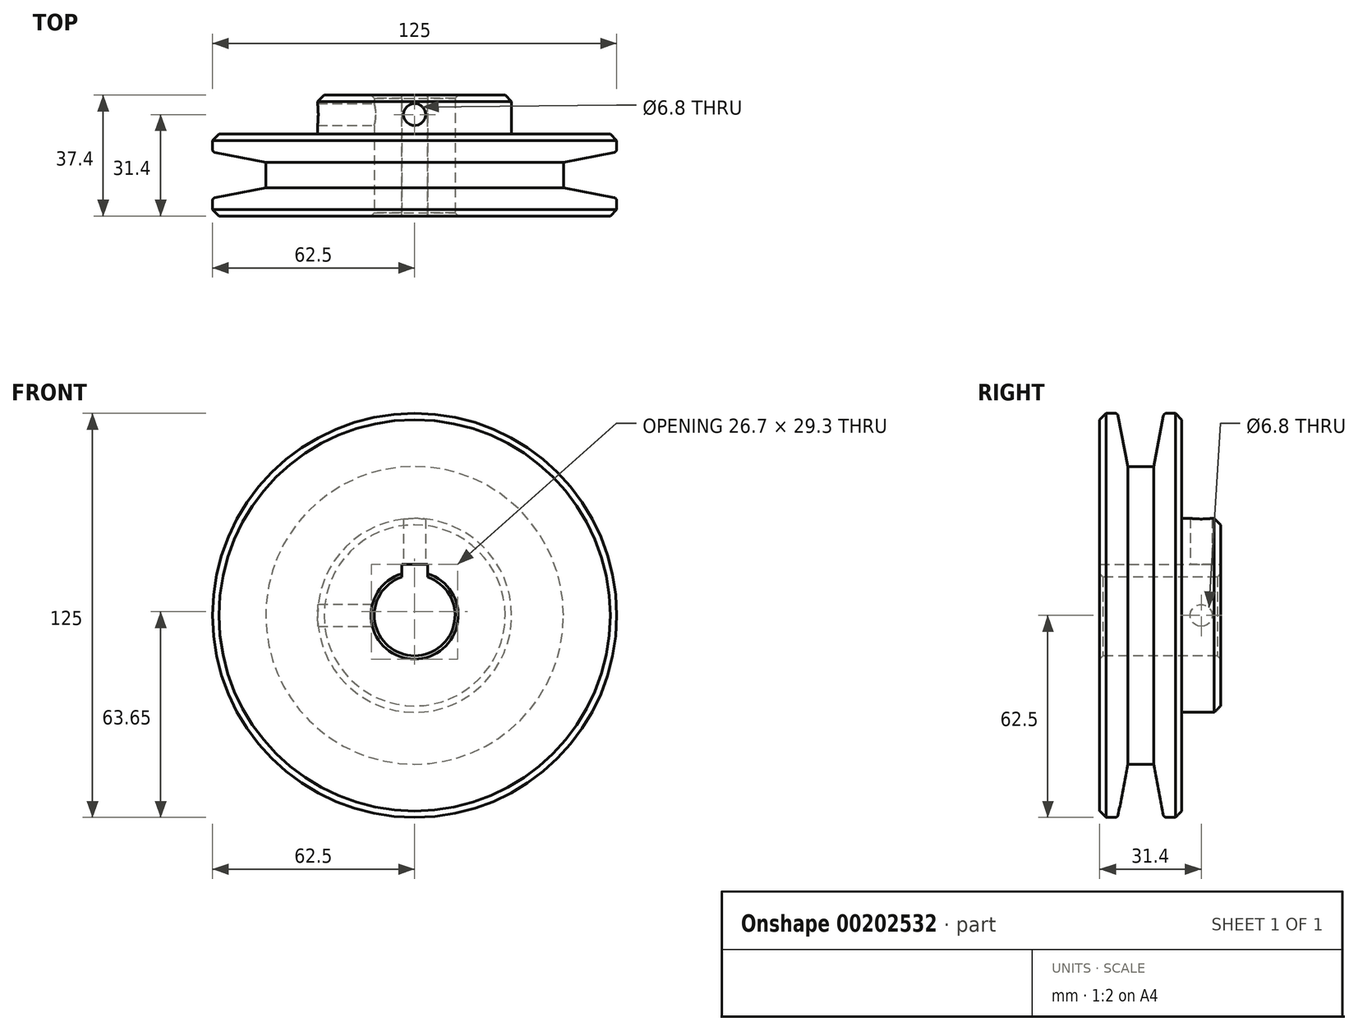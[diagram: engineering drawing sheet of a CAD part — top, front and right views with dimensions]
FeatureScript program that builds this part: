
annotation { "Feature Type Name" : "Feature", "Feature Type Description" : "" }
export const myFeature = defineFeature(function(context is Context, id is Id, definition is map)
    precondition{}
    {
        {
            var Q0;
            Q0=qCreatedBy(makeId("Right.planeOp"),FACE);
            var sketch = newSketch(context, id + "F0", { "sketchPlane" : qUnion([Q0])});
            skLineSegment(sketch, "E0", {"start": v(0, 64.09) * mm, "end": v(0, -58.72) * mm, "construction": true});
            skLineSegment(sketch, "E1", {"start": v(-33.32, 0) * mm, "end": v(29.36, 0) * mm, "construction": true});
            skLineSegment(sketch, "E2.bottom", {"start": v(-12.7, 12.5) * mm, "end": v(12.7, 12.5) * mm});
            skLineSegment(sketch, "E2.left", {"start": v(-12.7, 12.5) * mm, "end": v(-12.7, 62.5) * mm});
            skLineSegment(sketch, "E2.right", {"start": v(12.7, 30) * mm, "end": v(12.7, 62.5) * mm});
            skLineSegment(sketch, "E3.bottom", {"start": v(12.7, 12.5) * mm, "end": v(24.7, 12.5) * mm});
            skLineSegment(sketch, "E3.top", {"start": v(12.7, 30) * mm, "end": v(24.7, 30) * mm});
            skLineSegment(sketch, "E3.right", {"start": v(24.7, 12.5) * mm, "end": v(24.7, 30) * mm});
            skLineSegment(sketch, "E4", {"start": v(-6.99, 61.69) * mm, "end": v(-3.97, 46.04) * mm});
            skLineSegment(sketch, "E5", {"start": v(-3.97, 46.04) * mm, "end": v(0, 46.04) * mm});
            skLineSegment(sketch, "E6.MirrorCS", {"start": v(3.97, 46.04) * mm, "end": v(0, 46.04) * mm});
            skLineSegment(sketch, "E7.MirrorCS", {"start": v(6.99, 61.69) * mm, "end": v(3.97, 46.04) * mm});
            skLineSegment(sketch, "E8.trimOffspring", {"start": v(7.97, 62.5) * mm, "end": v(12.7, 62.5) * mm});
            skLineSegment(sketch, "E9", {"start": v(-12.7, 62.5) * mm, "end": v(-7.97, 62.5) * mm});
            skPoint(sketch, "E10.visualSharp", {"position": v(7.14, 62.5) * mm});
            skArc(sketch, "E10.filletArc", {"start": v(7.97, 62.5) * mm, "mid": v(7.33, 62.27) * mm, "end": v(6.99, 61.69) * mm});
            skPoint(sketch, "E11.visualSharp", {"position": v(-7.14, 62.5) * mm});
            skArc(sketch, "E11.filletArc", {"start": v(-6.99, 61.69) * mm, "mid": v(-7.33, 62.27) * mm, "end": v(-7.97, 62.5) * mm});
            skSolve(sketch);
        }
        {
            var Q0;
            Q0=makeQuery(id+"F0.imprint","IMPRINT",FACE,{"disambiguationData":[TD([[makeQuery(id+"F0.imprint","IMPRINT",EDGE,{"derivedFrom":sQuery(id+"F0.wireOp",EDGE,"E2.bottom")}),1.0]])]});
            var Q1;
            Q1=sQuery(id+"F0.wireOp",EDGE,"E1");
            revolve(context, id + "F1", {"entities" : qUnion([Q0]), "axis" : qUnion([Q1]), "revolveType" : RevolveType.FULL});
        }
        {
            var Q0;
            Q0=makeQuery(id+"F1.opRevolve","SWEPT_EDGE",EDGE,{"disambiguationData":[OSD([sQuery(id+"F0.wireOp",EDGE,"E2.right"),sQuery(id+"F0.wireOp",EDGE,"E8.trimOffspring")])]});
            chamfer(context, id + "F2", {"entities" : qUnion([Q0]), "width" : 2 * mm, "tangentPropagation" : true});
        }
        {
            var Q0;
            Q0=makeQuery(id+"F1.opRevolve","SWEPT_EDGE",EDGE,{"disambiguationData":[OSD([sQuery(id+"F0.wireOp",EDGE,"E2.left"),sQuery(id+"F0.wireOp",EDGE,"E9")])]});
            chamfer(context, id + "F3", {"entities" : qUnion([Q0]), "width" : 2 * mm, "tangentPropagation" : true});
        }
        {
            var Q0;
            Q0=makeQuery(id+"F1.opRevolve","SWEPT_FACE",FACE,{"disambiguationData":[OSD([sQuery(id+"F0.wireOp",EDGE,"E3.right")])]});
            var sketch = newSketch(context, id + "F4", { "sketchPlane" : qUnion([Q0])});
            skLineSegment(sketch, "E12", {"start": v(0, -1.06) * mm, "end": v(0, 35.19) * mm, "construction": true});
            skLineSegment(sketch, "E13.bottom", {"start": v(-4, 15.8) * mm, "end": v(4, 15.8) * mm});
            skLineSegment(sketch, "E13.top", {"start": v(-4, 9.2) * mm, "end": v(4, 9.2) * mm});
            skLineSegment(sketch, "E13.left", {"start": v(-4, 15.8) * mm, "end": v(-4, 9.2) * mm});
            skLineSegment(sketch, "E13.right", {"start": v(4, 15.8) * mm, "end": v(4, 9.2) * mm});
            skPoint(sketch, "E13.middle", {"position": v(0, 12.5) * mm});
            skSolve(sketch);
        }
        {
            var Q0;
            Q0 = qSketchRegion(id + "F4", true);
            extrude(context, id + "F5", {"entities" : qUnion([Q0]), "operationType" : NewBodyOperationType.REMOVE, "endBound" : BoundingType.THROUGH_ALL, "oppositeDirection" : true, "depth" : 25 * mm});
        }
        {
            var Q0;
            Q0=qCreatedBy(makeId("Top.planeOp"),FACE);
            var sketch = newSketch(context, id + "F6", { "sketchPlane" : qUnion([Q0])});
            skLineSegment(sketch, "E14", {"start": v(0, 0.74) * mm, "end": v(0, 36.66) * mm, "construction": true});
            skCircle(sketch, "E15", {"center": v(0, 18.7) * mm, "radius": 3.4 * mm});
            skSolve(sketch);
        }
        {
            var Q0;
            Q0 = qSketchRegion(id + "F6", true);
            extrude(context, id + "F7", {"entities" : qUnion([Q0]), "operationType" : NewBodyOperationType.REMOVE, "endBound" : BoundingType.THROUGH_ALL, "depth" : 25 * mm});
        }
        {
            var Q0;
            Q0=qCreatedBy(makeId("Right.planeOp"),FACE);
            var sketch = newSketch(context, id + "F8", { "sketchPlane" : qUnion([Q0])});
            skLineSegment(sketch, "E16", {"start": v(0, 0) * mm, "end": v(37.8, 0) * mm, "construction": true});
            skCircle(sketch, "E17", {"center": v(18.7, 0) * mm, "radius": 3.4 * mm});
            skSolve(sketch);
        }
        {
            var Q0;
            Q0 = qSketchRegion(id + "F8", true);
            extrude(context, id + "F9", {"entities" : qUnion([Q0]), "operationType" : NewBodyOperationType.REMOVE, "endBound" : BoundingType.THROUGH_ALL, "oppositeDirection" : true, "depth" : 25 * mm});
        }
        {
            var Q0;
            Q0=makeQuery(id+"F1.opRevolve","SWEPT_EDGE",EDGE,{"disambiguationData":[OSD([sQuery(id+"F0.wireOp",EDGE,"E3.bottom"),sQuery(id+"F0.wireOp",EDGE,"E3.right")])]});
            var Q1;
            Q1=makeQuery(id+"F1.opRevolve","SWEPT_EDGE",EDGE,{"disambiguationData":[OSD([sQuery(id+"F0.wireOp",EDGE,"E2.bottom"),sQuery(id+"F0.wireOp",EDGE,"E2.left")])]});
            chamfer(context, id + "F10", {"entities" : qUnion([Q0, Q1]), "width" : 1 * mm, "tangentPropagation" : true});
        }
        {
            var Q0;
            Q0=makeQuery(id+"F1.opRevolve","SWEPT_EDGE",EDGE,{"disambiguationData":[OSD([sQuery(id+"F0.wireOp",EDGE,"E3.top"),sQuery(id+"F0.wireOp",EDGE,"E3.right")])]});
            chamfer(context, id + "F11", {"entities" : qUnion([Q0]), "width" : 2 * mm, "tangentPropagation" : true});
        }
    });
